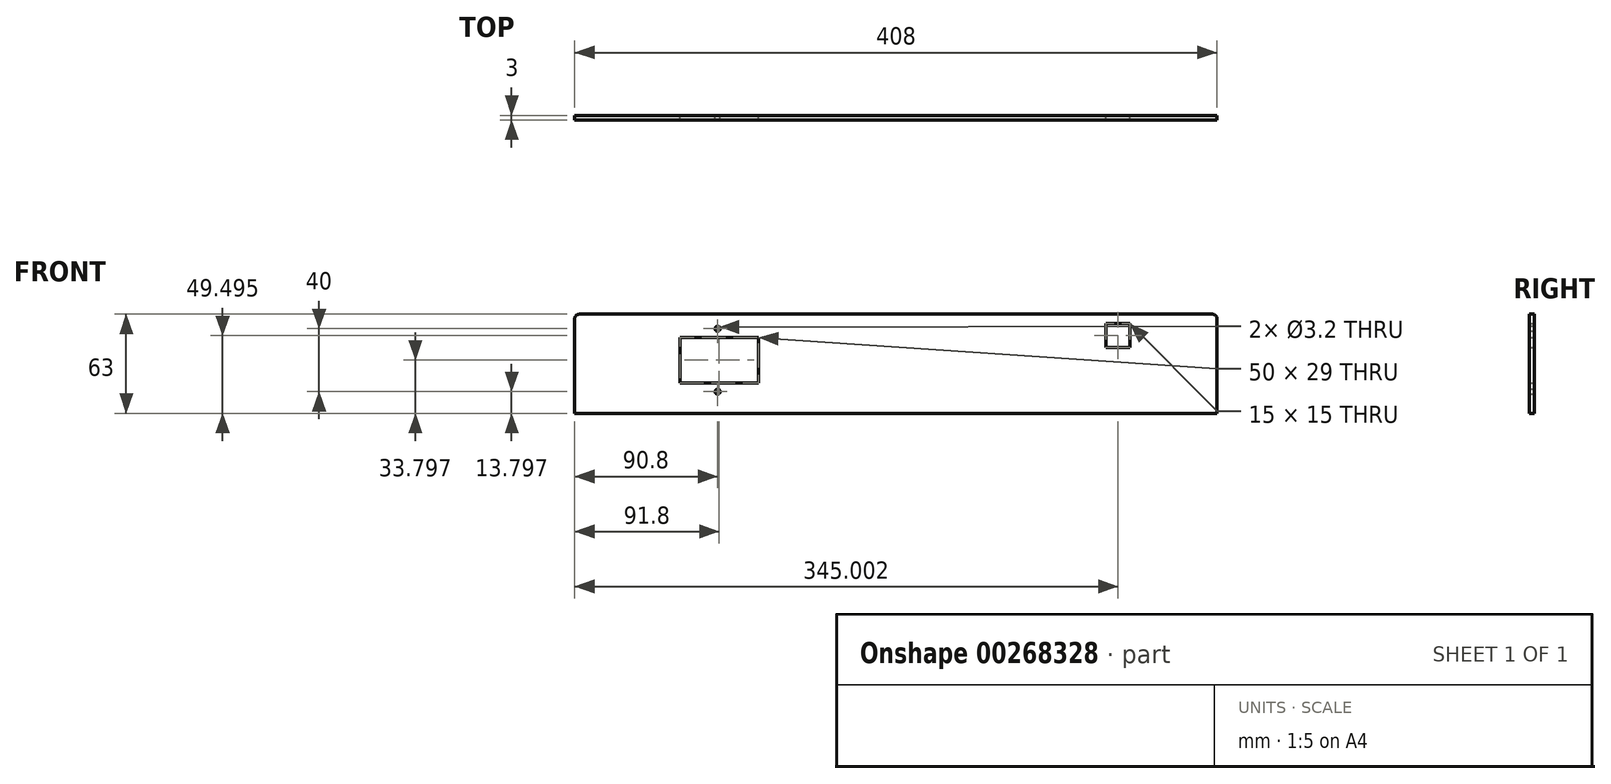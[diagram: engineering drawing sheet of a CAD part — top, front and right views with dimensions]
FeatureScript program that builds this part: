
annotation { "Feature Type Name" : "Feature", "Feature Type Description" : "" }
export const myFeature = defineFeature(function(context is Context, id is Id, definition is map)
    precondition{}
    {
        {
            var Q0;
            Q0=qCreatedBy(makeId("Front.planeOp"),FACE);
            var sketch = newSketch(context, id + "F0", { "sketchPlane" : qUnion([Q0])});
            skLineSegment(sketch, "E0.bottom", {"start": v(-225.79, -52.7) * mm, "end": v(176.21, -52.7) * mm});
            skLineSegment(sketch, "E0.top", {"start": v(-228.79, -115.7) * mm, "end": v(179.21, -115.7) * mm});
            skLineSegment(sketch, "E0.left", {"start": v(-228.79, -55.7) * mm, "end": v(-228.79, -115.7) * mm});
            skLineSegment(sketch, "E0.right", {"start": v(179.21, -55.7) * mm, "end": v(179.21, -115.7) * mm});
            skLineSegment(sketch, "E1.bottom", {"start": v(-162, -67.4) * mm, "end": v(-112, -67.4) * mm});
            skLineSegment(sketch, "E1.top", {"start": v(-162, -96.4) * mm, "end": v(-112, -96.4) * mm});
            skLineSegment(sketch, "E1.left", {"start": v(-162, -67.4) * mm, "end": v(-162, -96.4) * mm});
            skLineSegment(sketch, "E1.right", {"start": v(-112, -67.4) * mm, "end": v(-112, -96.4) * mm});
            skCircle(sketch, "E2", {"center": v(-138, -61.9) * mm, "radius": 1.6 * mm});
            skPoint(sketch, "E2.centerSnap0", {"position": v(-137, -67.4) * mm});
            skCircle(sketch, "E3", {"center": v(-138, -101.9) * mm, "radius": 1.6 * mm});
            skPoint(sketch, "E3.centerSnap0", {"position": v(-137, -96.4) * mm});
            skLineSegment(sketch, "E4.bottom", {"start": v(108.71, -58.7) * mm, "end": v(123.71, -58.7) * mm});
            skLineSegment(sketch, "E4.top", {"start": v(108.71, -73.7) * mm, "end": v(123.71, -73.7) * mm});
            skLineSegment(sketch, "E4.left", {"start": v(108.71, -58.7) * mm, "end": v(108.71, -73.7) * mm});
            skLineSegment(sketch, "E4.right", {"start": v(123.71, -58.7) * mm, "end": v(123.71, -73.7) * mm});
            skPoint(sketch, "E5.visualSharp", {"position": v(-228.79, -52.7) * mm});
            skArc(sketch, "E5.filletArc", {"start": v(-225.79, -52.7) * mm, "mid": v(-227.9, -53.57) * mm, "end": v(-228.79, -55.7) * mm});
            skPoint(sketch, "E6.visualSharp", {"position": v(179.21, -52.7) * mm});
            skArc(sketch, "E6.filletArc", {"start": v(179.21, -55.7) * mm, "mid": v(178.33, -53.57) * mm, "end": v(176.21, -52.7) * mm});
            skPoint(sketch, "E7.centerSnap0", {"position": v(179.21, -85.7) * mm});
            skLineSegment(sketch, "E8", {"start": v(-162, -81.9) * mm, "end": v(-112, -81.9) * mm, "construction": true});
            skSolve(sketch);
        }
        {
            var Q0;
            Q0=qSketchRegion(id+"F0",true);
            extrude(context, id + "F1", {"entities" : qUnion([Q0]), "depth" : 3 * mm});
        }
    });
